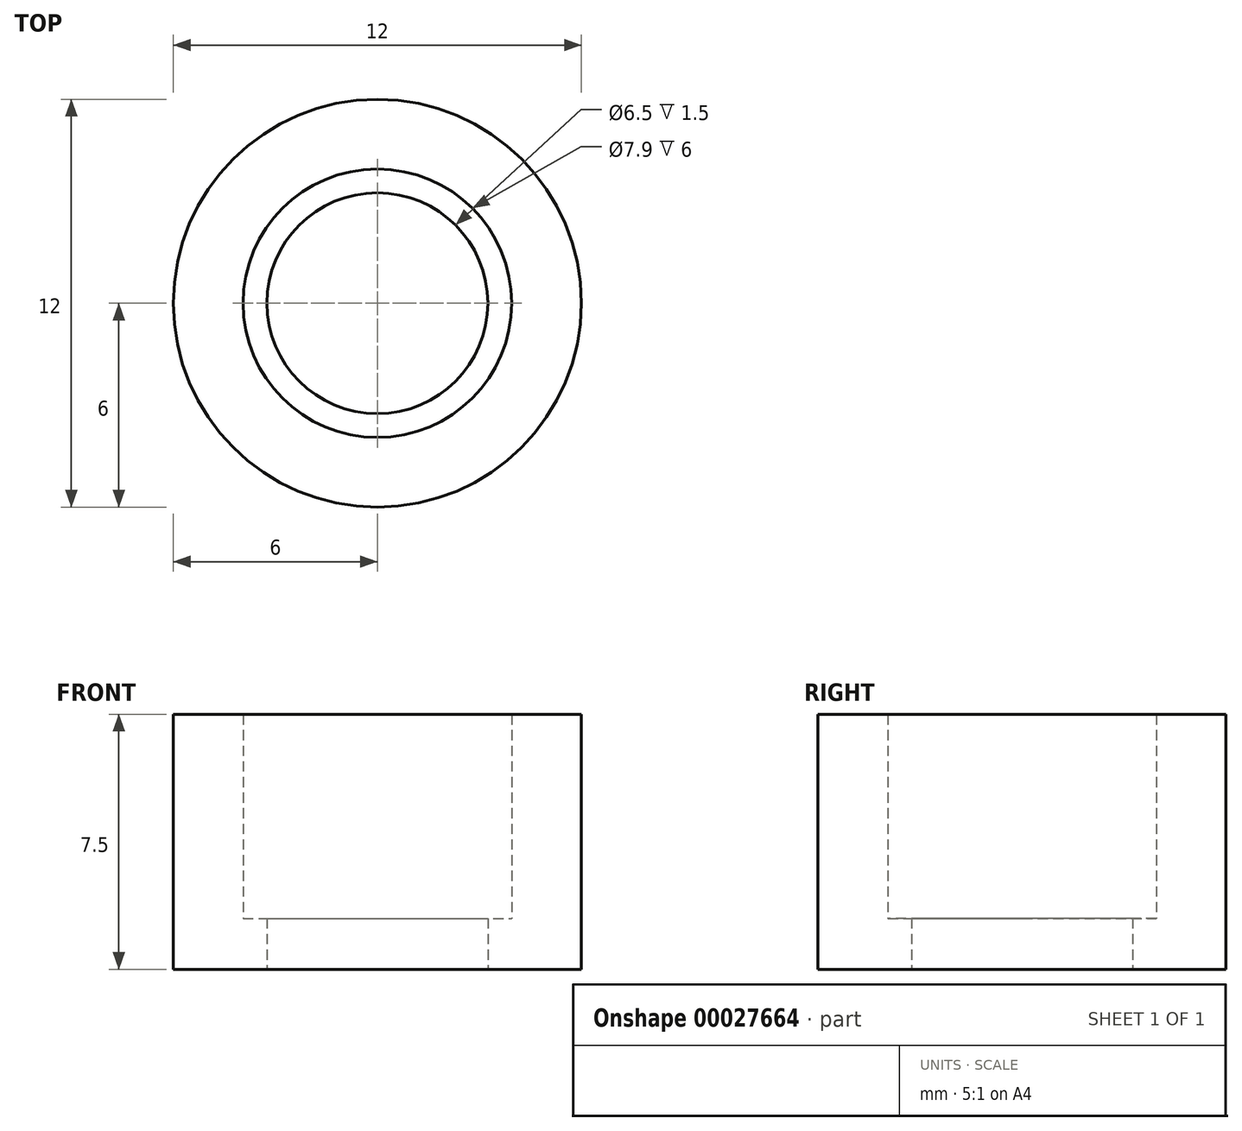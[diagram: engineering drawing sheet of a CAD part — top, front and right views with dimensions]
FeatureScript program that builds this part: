
annotation { "Feature Type Name" : "Feature", "Feature Type Description" : "" }
export const myFeature = defineFeature(function(context is Context, id is Id, definition is map)
    precondition{}
    {
        {
            var Q0;
            Q0=qCreatedBy(makeId("Front.planeOp"),FACE);
            var sketch = newSketch(context, id + "F0", { "sketchPlane" : qUnion([Q0])});
            skLineSegment(sketch, "E0", {"start": v(0, 0) * mm, "end": v(0, 21.33) * mm, "construction": true});
            skLineSegment(sketch, "E1", {"start": v(3.25, 0) * mm, "end": v(3.25, 1.5) * mm});
            skLineSegment(sketch, "E2", {"start": v(3.25, 1.5) * mm, "end": v(3.95, 1.5) * mm});
            skLineSegment(sketch, "E3", {"start": v(3.95, 1.5) * mm, "end": v(3.95, 7.5) * mm});
            skLineSegment(sketch, "E4", {"start": v(3.95, 7.5) * mm, "end": v(6, 7.5) * mm});
            skLineSegment(sketch, "E5", {"start": v(6, 7.5) * mm, "end": v(6, 0) * mm});
            skLineSegment(sketch, "E6", {"start": v(6, 0) * mm, "end": v(3.25, 0) * mm});
            skSolve(sketch);
        }
        {
            var Q0;
            Q0 = qSketchRegion(id + "F0", true);
            var Q1;
            Q1=sQuery(id+"F0.wireOp",EDGE,"E0");
            revolve(context, id + "F1", {"entities" : qUnion([Q0]), "axis" : qUnion([Q1]), "revolveType" : RevolveType.FULL});
        }
    });
